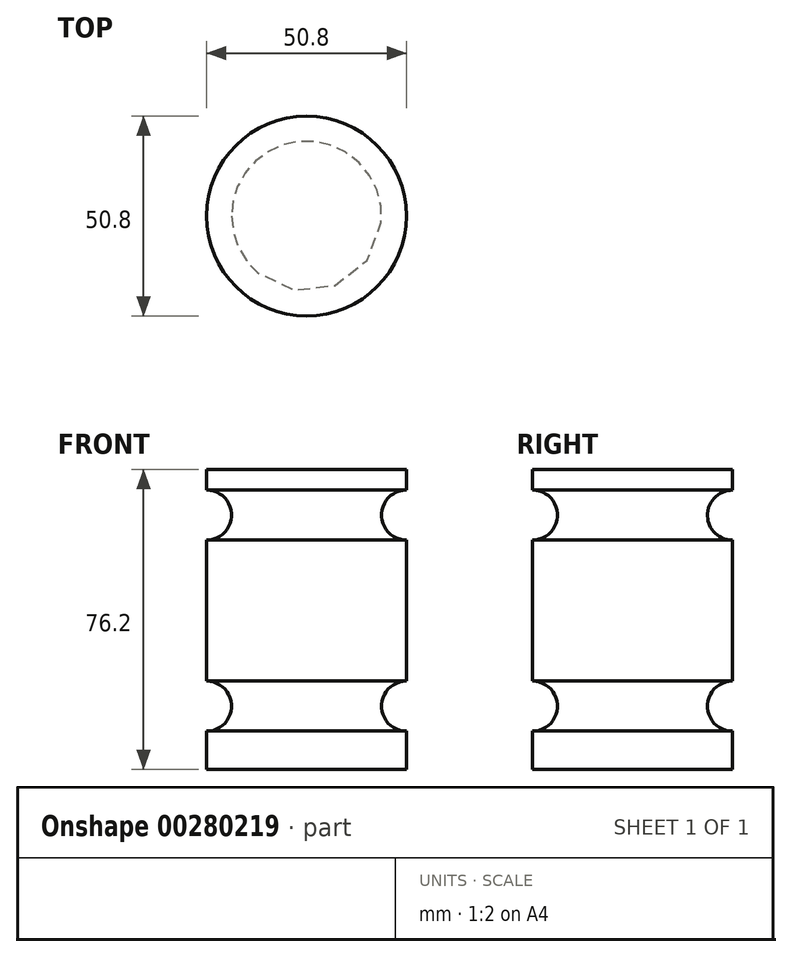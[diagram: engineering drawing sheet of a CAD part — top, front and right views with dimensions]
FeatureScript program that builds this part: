
annotation { "Feature Type Name" : "Feature", "Feature Type Description" : "" }
export const myFeature = defineFeature(function(context is Context, id is Id, definition is map)
    precondition{}
    {
        {
            var Q0;
            Q0=qCreatedBy(makeId("Front.planeOp"),FACE);
            var sketch = newSketch(context, id + "F0", { "sketchPlane" : qUnion([Q0])});
            skLineSegment(sketch, "E0.bottom", {"start": v(0, 0) * mm, "end": v(-25.4, 0) * mm});
            skLineSegment(sketch, "E0.top", {"start": v(0, 76.2) * mm, "end": v(-25.4, 76.2) * mm});
            skLineSegment(sketch, "E0.left", {"start": v(0, 0) * mm, "end": v(0, 9.73) * mm});
            skLineSegment(sketch, "E0.right", {"start": v(-25.4, 0) * mm, "end": v(-25.4, 76.2) * mm});
            skArc(sketch, "E1", {"start": v(0, 22.43) * mm, "mid": v(-6.35, 16.08) * mm, "end": v(0, 9.73) * mm});
            skLineSegment(sketch, "E2", {"start": v(0, 70.97) * mm, "end": v(0, 76.2) * mm});
            skArc(sketch, "E3", {"start": v(0, 70.97) * mm, "mid": v(-6.35, 64.62) * mm, "end": v(0, 58.27) * mm});
            skLineSegment(sketch, "E4", {"start": v(0, 22.43) * mm, "end": v(0, 58.27) * mm});
            skSolve(sketch);
        }
        {
            var Q0;
            Q0 = qSketchRegion(id + "F0", true);
            var Q1;
            Q1=sQuery(id+"F0.wireOp",EDGE,"E0.right");
            revolve(context, id + "F1", {"entities" : qUnion([Q0]), "axis" : qUnion([Q1]), "revolveType" : RevolveType.FULL});
        }
    });
